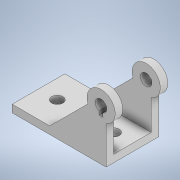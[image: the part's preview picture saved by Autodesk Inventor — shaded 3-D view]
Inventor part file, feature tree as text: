
AUTODESK INVENTOR PART (.ipt)
format: ipt  version: 2020 (Build 240168000, 168)  size: 300,032 bytes
history: native  units: mm
features: sketch x4, extrude x3, other x1, mirror x1, hole x1
ambient origin geometry x8: Origin, YZ Plane, XZ Plane, XY Plane, X Axis, Y Axis, Z Axis, Center Point
bodies: Body1 (feature_tree)
feature tree (10):
  other  "솔리드1"
  extrude  "돌출1"  Depth=30.0mm
  extrude  "돌출2"  Depth=30.0mm
  mirror  "미러1"
  hole  "구멍1"  [1 undecoded]
  extrude  "돌출3"  Depth=6.1mm
  sketch  "스케치1"
  sketch  "스케치2"
  sketch  "스케치3"
  sketch  "스케치4"
note: 1 required parameter value undecoded (feature->parameter linkage not recoverable at this tier; creation-order binding heuristic only, values carry confidence <= 0.55)
